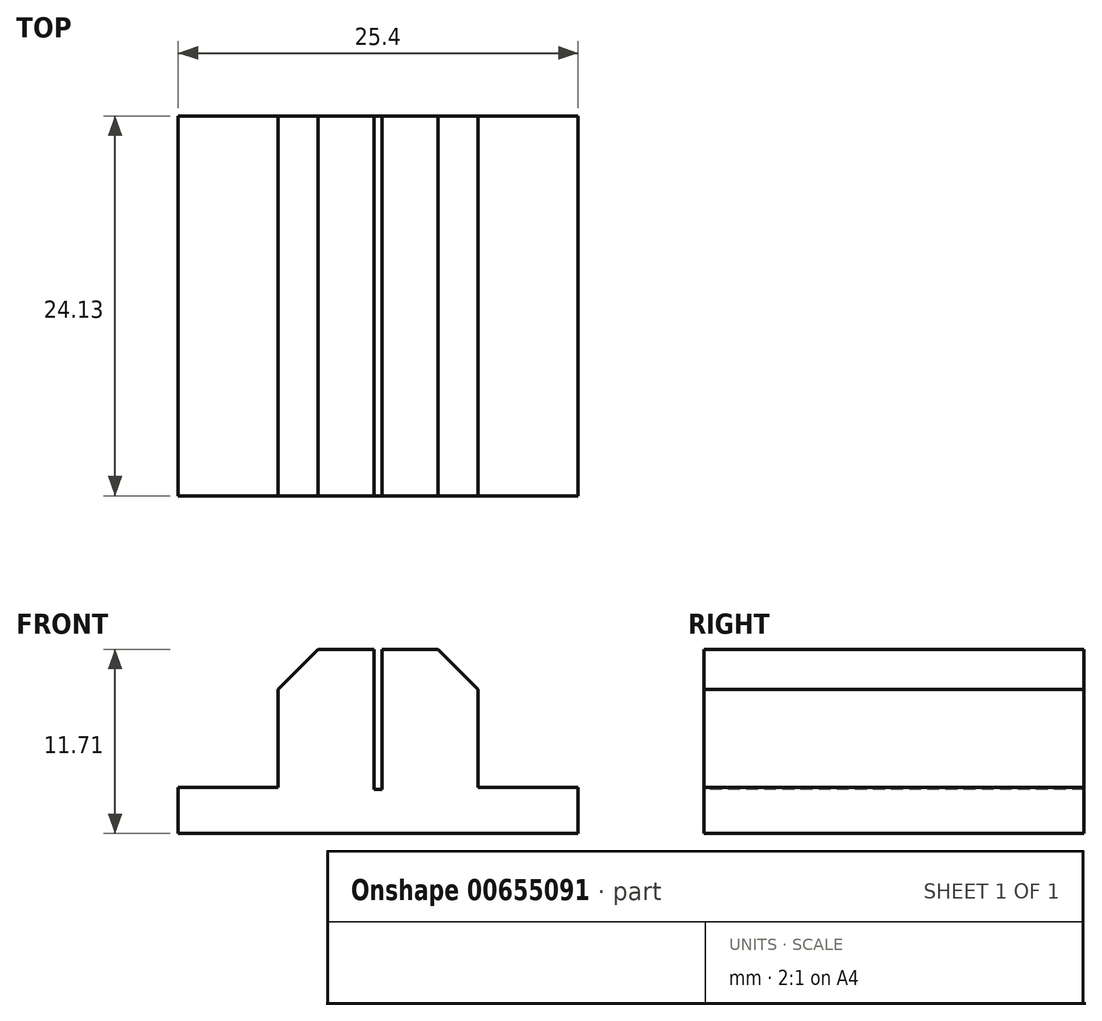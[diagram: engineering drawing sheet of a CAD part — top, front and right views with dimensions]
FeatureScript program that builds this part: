
annotation { "Feature Type Name" : "Feature", "Feature Type Description" : "" }
export const myFeature = defineFeature(function(context is Context, id is Id, definition is map)
    precondition{}
    {
        {
            var Q0;
            Q0=qCreatedBy(makeId("Front.planeOp"),FACE);
            var sketch = newSketch(context, id + "F0", { "sketchPlane" : qUnion([Q0])});
            skLineSegment(sketch, "E0.bottom", {"start": v(-12.7, -0.45) * mm, "end": v(12.7, -0.45) * mm});
            skLineSegment(sketch, "E0.top", {"start": v(-12.7, 2.48) * mm, "end": v(12.7, 2.48) * mm});
            skLineSegment(sketch, "E0.left", {"start": v(-12.7, -0.45) * mm, "end": v(-12.7, 2.48) * mm});
            skLineSegment(sketch, "E0.right", {"start": v(12.7, -0.45) * mm, "end": v(12.7, 2.48) * mm});
            skLineSegment(sketch, "E1.bottom", {"start": v(-6.35, 2.48) * mm, "end": v(6.35, 2.48) * mm});
            skLineSegment(sketch, "E1.top", {"start": v(-6.35, 11.26) * mm, "end": v(6.35, 11.26) * mm});
            skLineSegment(sketch, "E1.left", {"start": v(-6.35, 2.48) * mm, "end": v(-6.35, 11.26) * mm});
            skLineSegment(sketch, "E1.right", {"start": v(6.35, 2.48) * mm, "end": v(6.35, 11.26) * mm});
            skSolve(sketch);
        }
        {
            var Q0;
            Q0 = qSketchRegion(id + "F0", true);
            extrude(context, id + "F1", {"entities" : qUnion([Q0]), "depth" : 24.13 * mm, "offsetDistance" : 25.4 * mm});
        }
        {
            var Q0;
            Q0=makeQuery(id+"F1.opExtrude","SWEPT_FACE",FACE,{"disambiguationData":[OSD([sQuery(id+"F0.wireOp",EDGE,"E1.top")])]});
            var sketch = newSketch(context, id + "F2", { "sketchPlane" : qUnion([Q0])});
            skLineSegment(sketch, "E2.bottom", {"start": v(-0.25, 0) * mm, "end": v(0.25, 0) * mm});
            skLineSegment(sketch, "E2.top", {"start": v(-0.25, -24.13) * mm, "end": v(0.25, -24.13) * mm});
            skLineSegment(sketch, "E2.left", {"start": v(-0.25, 0) * mm, "end": v(-0.25, -24.13) * mm});
            skLineSegment(sketch, "E2.right", {"start": v(0.25, 0) * mm, "end": v(0.25, -24.13) * mm});
            skSolve(sketch);
        }
        {
            var Q0;
            Q0 = qSketchRegion(id + "F2", true);
            extrude(context, id + "F3", {"entities" : qUnion([Q0]), "operationType" : NewBodyOperationType.REMOVE, "oppositeDirection" : true, "depth" : 8.9 * mm, "offsetDistance" : 25.4 * mm});
        }
        {
            var Q0;
            Q0=makeQuery(id+"F1.opExtrude","SWEPT_EDGE",EDGE,{"disambiguationData":[OSD([sQuery(id+"F0.wireOp",EDGE,"E1.top"),sQuery(id+"F0.wireOp",EDGE,"E1.left")])]});
            var Q1;
            Q1=makeQuery(id+"F1.opExtrude","SWEPT_EDGE",EDGE,{"disambiguationData":[OSD([sQuery(id+"F0.wireOp",EDGE,"E1.top"),sQuery(id+"F0.wireOp",EDGE,"E1.right")])]});
            chamfer(context, id + "F4", {"entities" : qUnion([Q0, Q1]), "width" : 2.54 * mm, "tangentPropagation" : true});
        }
    });
